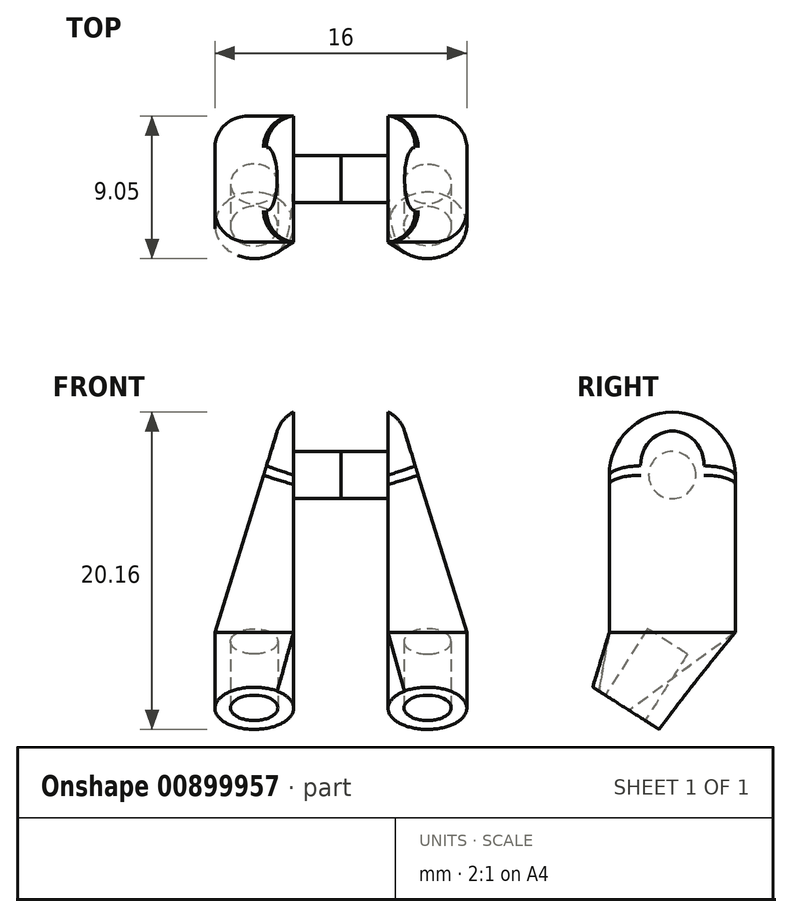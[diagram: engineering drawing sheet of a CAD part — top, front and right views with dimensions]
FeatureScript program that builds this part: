
annotation { "Feature Type Name" : "Feature", "Feature Type Description" : "" }
export const myFeature = defineFeature(function(context is Context, id is Id, definition is map)
    precondition{}
    {
        {
            var Q0;
            Q0=qCreatedBy(makeId("Right.planeOp"),FACE);
            var sketch = newSketch(context, id + "F0", { "sketchPlane" : qUnion([Q0])});
            skCircle(sketch, "E0", {"center": v(0, 0) * mm, "radius": 1.5 * mm});
            skSolve(sketch);
        }
        {
            var Q0;
            Q0 = qSketchRegion(id + "F0", true);
            extrude(context, id + "F1", {"entities" : qUnion([Q0]), "depth" : 3 * mm, "offsetDistance" : 25 * mm});
        }
        {
            var Q0;
            Q0=makeQuery(id+"F1.opExtrude","CAP_FACE",FACE,{"disambiguationData":[OSD([sQuery(id+"F0.wireOp",EDGE,"E0")])],"isStart":false});
            var sketch = newSketch(context, id + "F2", { "sketchPlane" : qUnion([Q0])});
            skArc(sketch, "E1", {"start": v(4, 0) * mm, "mid": v(0, 4) * mm, "end": v(-4, 0) * mm});
            skLineSegment(sketch, "E2.top", {"start": v(-4, -10) * mm, "end": v(4, -10) * mm});
            skLineSegment(sketch, "E2.left", {"start": v(-4, 0) * mm, "end": v(-4, -10) * mm});
            skLineSegment(sketch, "E2.right", {"start": v(4, 0) * mm, "end": v(4, -10) * mm});
            skPoint(sketch, "E2.middle", {"position": v(0, -5) * mm});
            skLineSegment(sketch, "E3", {"start": v(4, -10) * mm, "end": v(-0.18, -16.57) * mm, "construction": true});
            skLineSegment(sketch, "E4", {"start": v(-0.18, -16.57) * mm, "end": v(-5.88, -12.95) * mm, "construction": true});
            skLineSegment(sketch, "E5", {"start": v(-5.88, -12.95) * mm, "end": v(-4, -10) * mm, "construction": true});
            skLineSegment(sketch, "E6", {"start": v(-3.03, -14.76) * mm, "end": v(-1.45, -12.29) * mm, "construction": true});
            skSolve(sketch);
        }
        {
            var Q0;
            Q0 = qSketchRegion(id + "F2", true);
            extrude(context, id + "F3", {"entities" : qUnion([Q0]), "operationType" : NewBodyOperationType.ADD, "depth" : 5 * mm, "offsetDistance" : 25 * mm});
        }
        {
            var Q0;
            Q0=makeQuery(id+"F3.opExtrude","SWEPT_FACE",FACE,{"disambiguationData":[OSD([sQuery(id+"F2.wireOp",EDGE,"E2.left")])]});
            var sketch = newSketch(context, id + "F4", { "sketchPlane" : qUnion([Q0])});
            skLineSegment(sketch, "E7", {"start": v(8, -10) * mm, "end": v(3.52, 4.46) * mm});
            skLineSegment(sketch, "E8", {"start": v(3.52, 4.46) * mm, "end": v(8.5, 4.46) * mm});
            skLineSegment(sketch, "E9", {"start": v(8.5, 4.46) * mm, "end": v(8, -10) * mm});
            skSolve(sketch);
        }
        {
            var Q0;
            Q0 = qSketchRegion(id + "F4", true);
            extrude(context, id + "F5", {"entities" : qUnion([Q0]), "operationType" : NewBodyOperationType.REMOVE, "oppositeDirection" : true, "depth" : 25 * mm, "offsetDistance" : 25 * mm});
        }
        {
            var Q0;
            Q0=makeQuery(id+"F5.boolean.opBoolean","COPY",EDGE,{"derivedFrom":makeQuery(id+"F5.opExtrude","CAP_EDGE",EDGE,{"disambiguationData":[OSD([sQuery(id+"F4.wireOp",EDGE,"E7")])],"isStart":true})});
            var Q1;
            Q1=makeQuery(id+"F5.boolean.opBoolean","INTERSECT",EDGE,{"derivedFrom":[makeQuery(id+"F3.opExtrude","SWEPT_FACE",FACE,{"disambiguationData":[OSD([sQuery(id+"F2.wireOp",EDGE,"E1")])]}),makeQuery(id+"F5.opExtrude","SWEPT_FACE",FACE,{"disambiguationData":[OSD([sQuery(id+"F4.wireOp",EDGE,"E7")])]})]});
            fillet(context, id + "F6", {"entities" : qUnion([Q0, Q1]), "radius" : 2 * mm, "tangentPropagation" : true, "allowEdgeOverflow" : false});
        }
        {
            var Q0;
            Q0=sQuery(id+"F2.wireOp",VERTEX,"E4.end");
            var Q1;
            Q1=sQuery(id+"F2.wireOp",EDGE,"E5");
            cPlane(context, id + "F7", {"entities" : qUnion([Q0, Q1]), "cplaneType" : CPlaneType.LINE_POINT, "offset" : 25 * mm, "width" : 150 * mm, "height" : 150 * mm});
        }
        {
            var Q0;
            Q0=qCreatedBy(id+"F7.planeOp",FACE);
            var sketch = newSketch(context, id + "F8", { "sketchPlane" : qUnion([Q0])});
            skLineSegment(sketch, "E10", {"start": v(3, 5.46) * mm, "end": v(8, 5.46) * mm, "construction": true});
            skCircle(sketch, "E11", {"center": v(5.5, 5.46) * mm, "radius": 2.5 * mm});
            skSolve(sketch);
        }
        {
            var Q1;
            Q1=makeQuery(id+"F3.opExtrude","SWEPT_FACE",FACE,{"disambiguationData":[OSD([sQuery(id+"F2.wireOp",EDGE,"E2.top")])]});
            var Q2;
            Q2=makeQuery(id+"F8.imprint","IMPRINT",FACE,{"disambiguationData":[TD([[makeQuery(id+"F8.imprint","IMPRINT",EDGE,{"derivedFrom":sQuery(id+"F8.wireOp",EDGE,"E11")}),1.0]])]});
            loft(context, id + "F9", {"operationType" : NewBodyOperationType.ADD, "sheetProfilesArray" : [{ "sheetProfileEntities" : qUnion([Q1]) }, { "sheetProfileEntities" : qUnion([Q2]) }]});
        }
        {
            var Q0;
            Q0=makeQuery(id+"F9.opLoft","CAP_FACE",FACE,{"disambiguationData":[OSD([makeQuery(id+"F8.imprint","IMPRINT",FACE,{"disambiguationData":[TD([[makeQuery(id+"F8.imprint","IMPRINT",EDGE,{"derivedFrom":sQuery(id+"F8.wireOp",EDGE,"E11")}),1.0]])]})])],"isStart":true});
            var sketch = newSketch(context, id + "F10", { "sketchPlane" : qUnion([Q0])});
            skCircle(sketch, "E12", {"center": v(5.5, -5.4) * mm, "radius": 1.5 * mm});
            skSolve(sketch);
        }
        {
            var Q0;
            Q0=makeQuery(id+"F10.imprint","IMPRINT",FACE,{"disambiguationData":[TD([[makeQuery(id+"F10.imprint","IMPRINT",EDGE,{"derivedFrom":sQuery(id+"F10.wireOp",EDGE,"E12")}),1.0]])]});
            extrude(context, id + "F11", {"entities" : qUnion([Q0]), "operationType" : NewBodyOperationType.REMOVE, "oppositeDirection" : true, "depth" : 5 * mm, "offsetDistance" : 25 * mm});
        }
        {
            var Q0;
            Q0=makeQuery(id+"F1.opExtrude","SWEPT_BODY",BODY,{"disambiguationData":[OSD([sQuery(id+"F0.wireOp",EDGE,"E0")])]});
            var Q1;
            Q1=makeQuery(id+"F1.opExtrude","CAP_FACE",FACE,{"disambiguationData":[OSD([sQuery(id+"F0.wireOp",EDGE,"E0")])],"isStart":true});
            mirror(context, id + "F12", {"entities" : qUnion([Q0]), "mirrorPlane" : qUnion([Q1])});
        }
    });
